# Revit family: Door-Exterior-Simpson-Craftsman
name_source: partatom
category: Doors
revit_build: Autodesk Revit Architecture 2012 (Build: 20120126_0600(x64)
units: mm (PartAtom-declared; Revit-internal decimal feet)

## types (1)
- Door-Exterior-Simpson-Craftsman
    Assembly Code = B2020100
    Bottom Panel Height = 50 3/8"
    Bottom Rail Height = 9 3/16"
    Default Sill Height = 0"
    Description = Door
    Frame = Wood - Simpson Doors - Douglas Fir
    Frame Width = 3"
    Function = Exterior
    Glass = Glass - Simpson Doors - Clear
    Height = 84"
    Lock Rail Height = 7 3/8"
    Manufacturer = Simpson Door Company
    Model = 000
    Notes = Dozens of glass textures and colors are available. For a list of standard options visit the Simpson web site or submit a custom glass request.
    Number of Panel Dividers = 2
    Number of Vertical Muntins = 2
    Panel = Wood - Simpson Doors - Douglas Fir
    Panel Divider Width = 3 1/2"
    Panel Stile Width = 5"
    Panel Thickness = 3/4"
    Product Documentation Link = http://www.simpsondoor.com
    Product Page URL = http://www.simpsondoor.com
    Rough Height = 87"
    Rough Width = 42"
    SubSeries = Craftsman
    Thickness = 1 3/4"
    Top Rail Height = 5 15/16"
    URL = http://www.simpsondoor.com
    UltraBlock Note = This Door Comes with The Option of UltraBlock Technology. It is Turn On as a Default
    UltraBlock Option = Yes
    Wall Closure = Exterior
    WaterBarrier Note = This Door Comes with The Option of WaterBarrier with UltraBlock Technology. It is Turn Off as a Default
    WaterBarrier with UltraBlock Technology = No
    Width = 36"
    Window Height = 18 1/2"
    Wood Species = http://simpsondoor.com
    Wood Species Note = Available in Any Wood Species

## geometry (parser evidence)
native form markers: Blend x20, Sweep x19
no freeform markers — native parametric forms only
